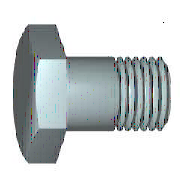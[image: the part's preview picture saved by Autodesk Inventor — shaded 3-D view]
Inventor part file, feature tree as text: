
AUTODESK INVENTOR PART (.ipt)
format: ipt  version: 2021 (Build 250183000, 183)  size: 200,192 bytes
history: native  units: mm (DEFAULTED — no unit token found)
features: sketch x3, extrude x1, chamfer x1, plane x1
ambient origin geometry x7: Origin, YZ Plane, XZ Plane, X Axis, Y Axis, Z Axis, Center Point
bodies: Solid1 (feature_tree), Body (feature_tree)
feature tree (6):
  extrude  "Head"  Depth=8.3mm
  chamfer  "Chamfer1"  Distance=4.7mm
  plane  "Work Plane1"
  sketch  "Sketch1"  dims[d0=12.0mm d1=8.3mm]
  sketch  "Sketch2"  dims[d2=8.0mm]
  sketch  "Sketch4"  dims[d12=90.0deg d3=4.7mm d4=0.0mm d5=30.0deg d21=90.0deg d6=0.766813mm d7=0.766912mm d8=0.0mm d9=0.6001mm d10=13.0mm d11=13.0mm d13=0.766912mm d14=8.0mm d15=8.3mm d16=0.0mm d19=13.0mm d55=45.0deg d57=0.0mm d58=0.0mm]
